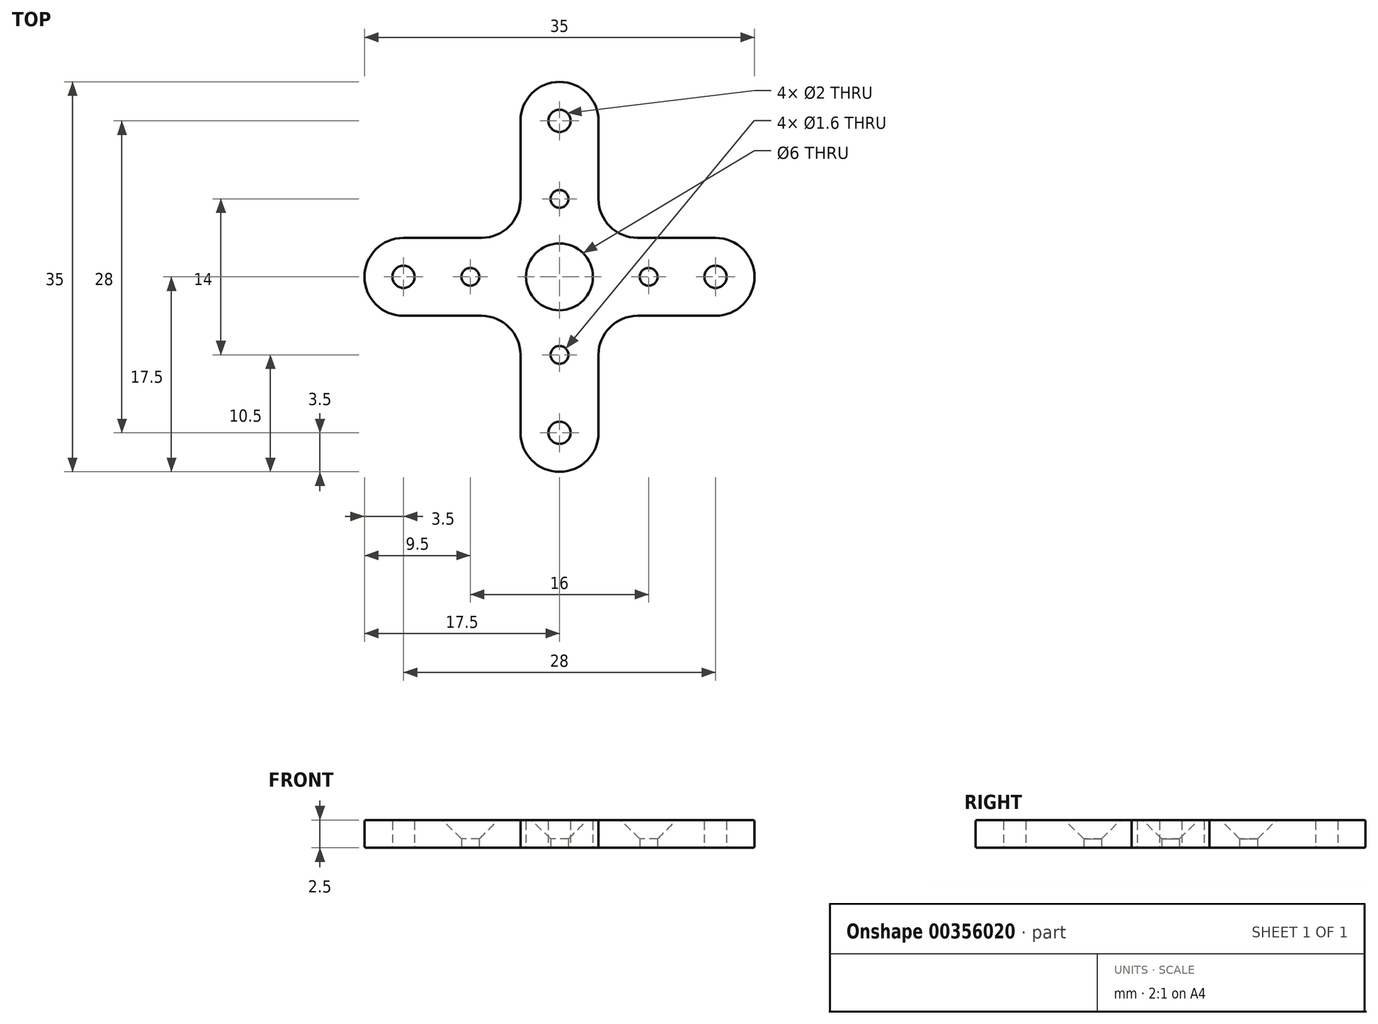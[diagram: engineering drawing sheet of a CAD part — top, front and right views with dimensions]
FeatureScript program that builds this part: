
annotation { "Feature Type Name" : "Feature", "Feature Type Description" : "" }
export const myFeature = defineFeature(function(context is Context, id is Id, definition is map)
    precondition{}
    {
        {
            var Q0;
            Q0=qCreatedBy(makeId("Top.planeOp"),FACE);
            var sketch = newSketch(context, id + "F0", { "sketchPlane" : qUnion([Q0])});
            skLineSegment(sketch, "E0.bottom", {"start": v(-17.84, -37.87) * mm, "end": v(-24.84, -37.87) * mm});
            skLineSegment(sketch, "E0.top", {"start": v(-17.84, -2.87) * mm, "end": v(-24.84, -2.87) * mm});
            skLineSegment(sketch, "E0.left", {"start": v(-3.84, -23.87) * mm, "end": v(-3.84, -16.87) * mm});
            skLineSegment(sketch, "E0.right", {"start": v(-38.84, -23.87) * mm, "end": v(-38.84, -16.87) * mm});
            skPoint(sketch, "E0.middle", {"position": v(-21.34, -20.37) * mm});
            skCircle(sketch, "E1", {"center": v(-21.34, -20.37) * mm, "radius": 3 * mm});
            skLineSegment(sketch, "E2", {"start": v(-38.84, -23.87) * mm, "end": v(-24.84, -23.87) * mm});
            skLineSegment(sketch, "E3", {"start": v(-24.84, -23.87) * mm, "end": v(-24.84, -37.87) * mm});
            skPoint(sketch, "E4.orphan", {"position": v(-38.84, -37.87) * mm});
            skLineSegment(sketch, "E5", {"start": v(-24.84, -2.87) * mm, "end": v(-24.84, -16.87) * mm});
            skLineSegment(sketch, "E6", {"start": v(-24.84, -16.87) * mm, "end": v(-38.84, -16.87) * mm});
            skLineSegment(sketch, "E7", {"start": v(-17.84, -2.87) * mm, "end": v(-17.84, -16.87) * mm});
            skLineSegment(sketch, "E8", {"start": v(-17.84, -16.87) * mm, "end": v(-3.84, -16.87) * mm});
            skLineSegment(sketch, "E9", {"start": v(-3.84, -23.87) * mm, "end": v(-17.84, -23.87) * mm});
            skLineSegment(sketch, "E10", {"start": v(-17.84, -23.87) * mm, "end": v(-17.84, -37.87) * mm});
            skPoint(sketch, "E11.orphan", {"position": v(-38.84, -2.87) * mm});
            skPoint(sketch, "E12.orphan", {"position": v(-3.84, -2.87) * mm});
            skPoint(sketch, "E13.orphan", {"position": v(-3.84, -37.87) * mm});
            skCircle(sketch, "E14", {"center": v(-7.34, -20.37) * mm, "radius": 1 * mm});
            skCircle(sketch, "E15", {"center": v(-35.34, -20.37) * mm, "radius": 1 * mm});
            skCircle(sketch, "E16", {"center": v(-21.34, -6.37) * mm, "radius": 1 * mm});
            skCircle(sketch, "E17", {"center": v(-21.34, -34.37) * mm, "radius": 1 * mm});
            skCircle(sketch, "E18", {"center": v(-13.34, -20.37) * mm, "radius": 0.8 * mm});
            skCircle(sketch, "E19", {"center": v(-29.34, -20.37) * mm, "radius": 0.8 * mm});
            skCircle(sketch, "E20", {"center": v(-21.34, -13.37) * mm, "radius": 0.8 * mm});
            skCircle(sketch, "E21", {"center": v(-21.34, -27.37) * mm, "radius": 0.8 * mm});
            skSolve(sketch);
        }
        {
            var Q0;
            Q0=makeQuery(id+"F0.imprint","IMPRINT",FACE,{"disambiguationData":[TD([[makeQuery(id+"F0.imprint","IMPRINT",EDGE,{"derivedFrom":sQuery(id+"F0.wireOp",EDGE,"E0.bottom")}),-1.0]])]});
            extrude(context, id + "F1", {"entities" : qUnion([Q0]), "depth" : 2.5 * mm});
        }
        {
            var Q0;
            Q0=makeQuery(id+"F1.opExtrude","SWEPT_EDGE",EDGE,{"disambiguationData":[OSD([sQuery(id+"F0.wireOp",EDGE,"E0.top"),sQuery(id+"F0.wireOp",EDGE,"E5")])]});
            var Q1;
            Q1=makeQuery(id+"F1.opExtrude","SWEPT_EDGE",EDGE,{"disambiguationData":[OSD([sQuery(id+"F0.wireOp",EDGE,"E0.top"),sQuery(id+"F0.wireOp",EDGE,"E7")])]});
            var Q2;
            Q2=makeQuery(id+"F1.opExtrude","SWEPT_EDGE",EDGE,{"disambiguationData":[OSD([sQuery(id+"F0.wireOp",EDGE,"E0.left"),sQuery(id+"F0.wireOp",EDGE,"E8")])]});
            var Q3;
            Q3=makeQuery(id+"F1.opExtrude","SWEPT_EDGE",EDGE,{"disambiguationData":[OSD([sQuery(id+"F0.wireOp",EDGE,"E0.left"),sQuery(id+"F0.wireOp",EDGE,"E9")])]});
            var Q4;
            Q4=makeQuery(id+"F1.opExtrude","SWEPT_EDGE",EDGE,{"disambiguationData":[OSD([sQuery(id+"F0.wireOp",EDGE,"E0.bottom"),sQuery(id+"F0.wireOp",EDGE,"E10")])]});
            var Q5;
            Q5=makeQuery(id+"F1.opExtrude","SWEPT_EDGE",EDGE,{"disambiguationData":[OSD([sQuery(id+"F0.wireOp",EDGE,"E0.bottom"),sQuery(id+"F0.wireOp",EDGE,"E3")])]});
            var Q6;
            Q6=makeQuery(id+"F1.opExtrude","SWEPT_EDGE",EDGE,{"disambiguationData":[OSD([sQuery(id+"F0.wireOp",EDGE,"E0.right"),sQuery(id+"F0.wireOp",EDGE,"E2")])]});
            var Q7;
            Q7=makeQuery(id+"F1.opExtrude","SWEPT_EDGE",EDGE,{"disambiguationData":[OSD([sQuery(id+"F0.wireOp",EDGE,"E0.right"),sQuery(id+"F0.wireOp",EDGE,"E6")])]});
            var Q8;
            Q8=makeQuery(id+"F1.opExtrude","SWEPT_EDGE",EDGE,{"disambiguationData":[OSD([sQuery(id+"F0.wireOp",EDGE,"E2"),sQuery(id+"F0.wireOp",EDGE,"E3")])]});
            var Q9;
            Q9=makeQuery(id+"F1.opExtrude","SWEPT_EDGE",EDGE,{"disambiguationData":[OSD([sQuery(id+"F0.wireOp",EDGE,"E9"),sQuery(id+"F0.wireOp",EDGE,"E10")])]});
            var Q10;
            Q10=makeQuery(id+"F1.opExtrude","SWEPT_EDGE",EDGE,{"disambiguationData":[OSD([sQuery(id+"F0.wireOp",EDGE,"E7"),sQuery(id+"F0.wireOp",EDGE,"E8")])]});
            var Q11;
            Q11=makeQuery(id+"F1.opExtrude","SWEPT_EDGE",EDGE,{"disambiguationData":[OSD([sQuery(id+"F0.wireOp",EDGE,"E5"),sQuery(id+"F0.wireOp",EDGE,"E6")])]});
            fillet(context, id + "F2", {"entities" : qUnion([Q0, Q1, Q2, Q3, Q4, Q5, Q6, Q7, Q8, Q9, Q10, Q11]), "radius" : 3.5 * mm, "tangentPropagation" : true, "allowEdgeOverflow" : false});
        }
        {
            var Q0;
            Q0=makeQuery(id+"F1.opExtrude","CAP_EDGE",EDGE,{"disambiguationData":[OSD([sQuery(id+"F0.wireOp",EDGE,"E20")])],"isStart":false});
            var Q1;
            Q1=makeQuery(id+"F1.opExtrude","CAP_EDGE",EDGE,{"disambiguationData":[OSD([sQuery(id+"F0.wireOp",EDGE,"E18")])],"isStart":false});
            var Q2;
            Q2=makeQuery(id+"F1.opExtrude","CAP_EDGE",EDGE,{"disambiguationData":[OSD([sQuery(id+"F0.wireOp",EDGE,"E21")])],"isStart":false});
            var Q3;
            Q3=makeQuery(id+"F1.opExtrude","CAP_EDGE",EDGE,{"disambiguationData":[OSD([sQuery(id+"F0.wireOp",EDGE,"E19")])],"isStart":false});
            chamfer(context, id + "F3", {"entities" : qUnion([Q0, Q1, Q2, Q3]), "width" : 1.7 * mm, "tangentPropagation" : true});
        }
        {
            var Q0;
            Q0=makeQuery(id+"F1.opExtrude","CAP_FACE",FACE,{"disambiguationData":[OSD([sQuery(id+"F0.wireOp",EDGE,"E0.bottom"),sQuery(id+"F0.wireOp",EDGE,"E0.top"),sQuery(id+"F0.wireOp",EDGE,"E0.left"),sQuery(id+"F0.wireOp",EDGE,"E0.right"),sQuery(id+"F0.wireOp",EDGE,"E1"),sQuery(id+"F0.wireOp",EDGE,"E2"),sQuery(id+"F0.wireOp",EDGE,"E3"),sQuery(id+"F0.wireOp",EDGE,"E5"),sQuery(id+"F0.wireOp",EDGE,"E6"),sQuery(id+"F0.wireOp",EDGE,"E7"),sQuery(id+"F0.wireOp",EDGE,"E8"),sQuery(id+"F0.wireOp",EDGE,"E9"),sQuery(id+"F0.wireOp",EDGE,"E10"),sQuery(id+"F0.wireOp",EDGE,"E14"),sQuery(id+"F0.wireOp",EDGE,"E15"),sQuery(id+"F0.wireOp",EDGE,"E16"),sQuery(id+"F0.wireOp",EDGE,"E17"),sQuery(id+"F0.wireOp",EDGE,"E18"),sQuery(id+"F0.wireOp",EDGE,"E19"),sQuery(id+"F0.wireOp",EDGE,"E20"),sQuery(id+"F0.wireOp",EDGE,"E21")])],"isStart":false});
            var Q1;
            Q1=makeQuery(id+"F1.opExtrude","CAP_FACE",FACE,{"disambiguationData":[OSD([sQuery(id+"F0.wireOp",EDGE,"E0.bottom"),sQuery(id+"F0.wireOp",EDGE,"E0.top"),sQuery(id+"F0.wireOp",EDGE,"E0.left"),sQuery(id+"F0.wireOp",EDGE,"E0.right"),sQuery(id+"F0.wireOp",EDGE,"E1"),sQuery(id+"F0.wireOp",EDGE,"E2"),sQuery(id+"F0.wireOp",EDGE,"E3"),sQuery(id+"F0.wireOp",EDGE,"E5"),sQuery(id+"F0.wireOp",EDGE,"E6"),sQuery(id+"F0.wireOp",EDGE,"E7"),sQuery(id+"F0.wireOp",EDGE,"E8"),sQuery(id+"F0.wireOp",EDGE,"E9"),sQuery(id+"F0.wireOp",EDGE,"E10"),sQuery(id+"F0.wireOp",EDGE,"E14"),sQuery(id+"F0.wireOp",EDGE,"E15"),sQuery(id+"F0.wireOp",EDGE,"E16"),sQuery(id+"F0.wireOp",EDGE,"E17"),sQuery(id+"F0.wireOp",EDGE,"E18"),sQuery(id+"F0.wireOp",EDGE,"E19"),sQuery(id+"F0.wireOp",EDGE,"E20"),sQuery(id+"F0.wireOp",EDGE,"E21")])],"isStart":true});
            fillet(context, id + "F4", {"entities" : qUnion([Q0, Q1]), "radius" : 0.15 * mm, "tangentPropagation" : true, "allowEdgeOverflow" : false});
        }
    });
